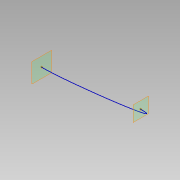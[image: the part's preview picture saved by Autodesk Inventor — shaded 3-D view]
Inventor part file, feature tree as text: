
AUTODESK INVENTOR PART (.ipt)
format: ipt  version: 2019 (Build 230136000, 136)  size: 87,552 bytes
history: native  units: mm
features: other x2, plane x2, sketch x1
ambient origin geometry x8: Origin, YZ Plane, XZ Plane, XY Plane, X Axis, Y Axis, Z Axis, Center Point
feature tree (5):
  other  "Punto de trabajo1"
  other  "Punto de trabajo2"
  plane  "Plano de trabajo1"
  plane  "Plano de trabajo2"
  sketch  "Boceto 3D1"  dims[d0=10.0mm d1=-0.1mm d2=-10.0mm d3=-0.1mm]
